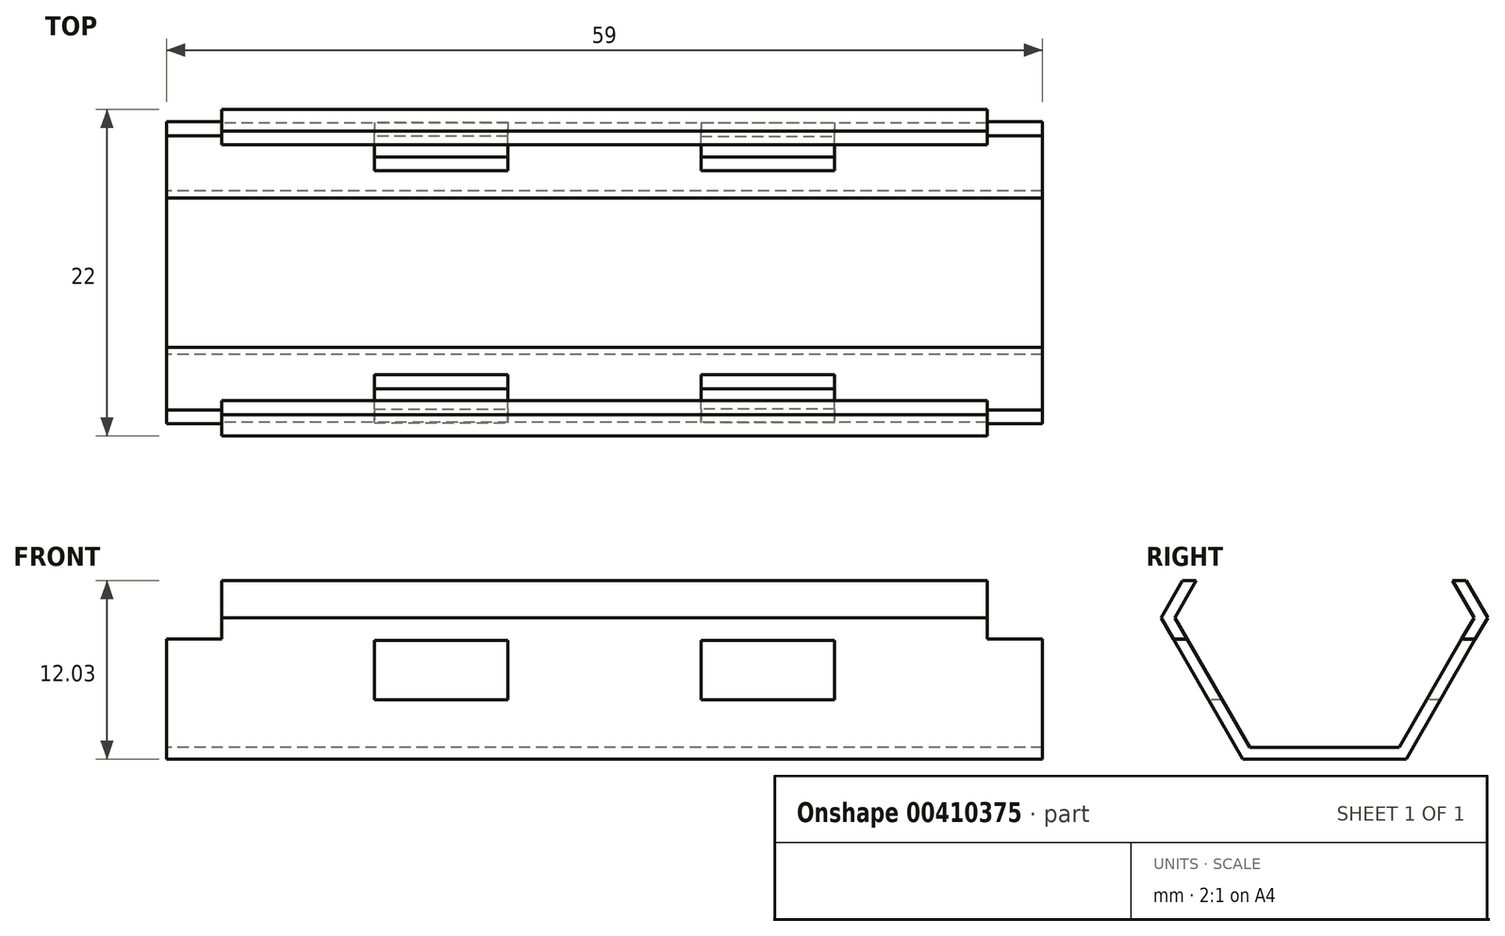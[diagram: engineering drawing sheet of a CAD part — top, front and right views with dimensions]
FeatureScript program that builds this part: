
annotation { "Feature Type Name" : "Feature", "Feature Type Description" : "" }
export const myFeature = defineFeature(function(context is Context, id is Id, definition is map)
    precondition{}
    {
        {
            var Q0;
            Q0=qCreatedBy(makeId("Right.planeOp"),FACE);
            var sketch = newSketch(context, id + "F0", { "sketchPlane" : qUnion([Q0])});
            skCircle(sketch, "E0.cCircle", {"center": v(0, 0) * mm, "radius": 9.53 * mm, "construction": true});
            skLineSegment(sketch, "E0.0", {"start": v(5.5, 9.53) * mm, "end": v(11, 0) * mm});
            skLineSegment(sketch, "E0.1", {"start": v(11, 0) * mm, "end": v(5.5, -9.53) * mm});
            skLineSegment(sketch, "E0.2", {"start": v(5.5, -9.53) * mm, "end": v(-5.5, -9.53) * mm});
            skLineSegment(sketch, "E0.3", {"start": v(-5.5, -9.53) * mm, "end": v(-11, 0) * mm});
            skLineSegment(sketch, "E0.4", {"start": v(-11, 0) * mm, "end": v(-5.5, 9.53) * mm});
            skLineSegment(sketch, "E0.5", {"start": v(-5.5, 9.53) * mm, "end": v(5.5, 9.53) * mm});
            skPoint(sketch, "E0.0.midPoint", {"position": v(8.25, 4.76) * mm});
            skSolve(sketch);
        }
        {
            var Q0;
            Q0=qCreatedBy(makeId("Right.planeOp"),FACE);
            var sketch = newSketch(context, id + "F1", { "sketchPlane" : qUnion([Q0])});
            skLineSegment(sketch, "E1.0", {"start": v(-10.08, 0) * mm, "end": v(-5.04, 8.73) * mm});
            skLineSegment(sketch, "E1.1", {"start": v(5.04, 8.73) * mm, "end": v(10.08, 0) * mm});
            skLineSegment(sketch, "E1.2", {"start": v(10.08, 0) * mm, "end": v(5.04, -8.73) * mm});
            skLineSegment(sketch, "E1.3", {"start": v(-5.04, 8.73) * mm, "end": v(5.04, 8.73) * mm});
            skLineSegment(sketch, "E1.4", {"start": v(5.04, -8.73) * mm, "end": v(-5.04, -8.73) * mm});
            skLineSegment(sketch, "E1.5", {"start": v(-5.04, -8.73) * mm, "end": v(-10.08, 0) * mm});
            skSolve(sketch);
        }
        {
            var Q0;
            Q0=makeQuery(id+"F0.imprint","IMPRINT",FACE,{"disambiguationData":[TD([[makeQuery(id+"F0.imprint","IMPRINT",EDGE,{"derivedFrom":sQuery(id+"F0.wireOp",EDGE,"E0.0")}),-1.0]])]});
            extrude(context, id + "F2", {"entities" : qUnion([Q0]), "endBound" : BoundingType.SYMMETRIC, "depth" : 59 * mm});
        }
        {
            var Q0;
            Q0 = qSketchRegion(id + "F1", true);
            extrude(context, id + "F3", {"entities" : qUnion([Q0]), "operationType" : NewBodyOperationType.REMOVE, "endBound" : BoundingType.SYMMETRIC, "depth" : 60 * mm});
        }
        {
            var Q0;
            Q0=makeQuery(id+"F0.imprint","IMPRINT",FACE,{"disambiguationData":[TD([[makeQuery(id+"F0.imprint","IMPRINT",EDGE,{"derivedFrom":sQuery(id+"F0.wireOp",EDGE,"E0.0")}),-1.0]])]});
            var sketch = newSketch(context, id + "F4", { "sketchPlane" : qUnion([Q0])});
            skLineSegment(sketch, "E2.bottom", {"start": v(-12.38, -9.5) * mm, "end": v(12.27, -9.5) * mm});
            skLineSegment(sketch, "E2.top", {"start": v(-12.38, 2.5) * mm, "end": v(12.27, 2.5) * mm});
            skLineSegment(sketch, "E2.left", {"start": v(-12.38, -9.5) * mm, "end": v(-12.38, 2.5) * mm});
            skLineSegment(sketch, "E2.right", {"start": v(12.27, -9.5) * mm, "end": v(12.27, 2.5) * mm});
            skPoint(sketch, "E3.MirrorCS.end.orphan", {"position": v(12.27, 2.5) * mm});
            skPoint(sketch, "E3.MirrorCS.start.orphan", {"position": v(36.91, 2.5) * mm});
            skLineSegment(sketch, "E4.MirrorCS", {"start": v(12.27, 14.5) * mm, "end": v(12.27, 2.5) * mm});
            skLineSegment(sketch, "E5.MirrorCS", {"start": v(-12.38, 14.5) * mm, "end": v(12.27, 14.5) * mm});
            skLineSegment(sketch, "E6.MirrorCS", {"start": v(-12.38, 14.5) * mm, "end": v(-12.38, 2.5) * mm});
            skSolve(sketch);
        }
        {
            var Q0;
            {var subQ4=sQuery(id+"F4.wireOp",EDGE,"E4.MirrorCS");Q0=makeQuery(id+"F4.imprint","IMPRINT",FACE,{"disambiguationData":[TD([[makeQuery(id+"F4.imprint","IMPRINT",EDGE,{"derivedFrom":subQ4}),-1.0]])]});}
            var Q1;
            {var subQ5=makeQuery(id+"F0.imprint","IMPRINT",EDGE,{"derivedFrom":sQuery(id+"F0.wireOp",EDGE,"E0.5")});Q1=makeQuery(id+"F4.imprint","IMPRINT",FACE,{"disambiguationData":[TD([[makeQuery(id+"F4.imprint","IMPRINT",EDGE,{"derivedFrom":subQ5}),-1.0]])]});}
            extrude(context, id + "F5", {"entities" : qUnion([Q0, Q1]), "operationType" : NewBodyOperationType.REMOVE, "endBound" : BoundingType.SYMMETRIC, "depth" : 91.7 * mm});
        }
        {
            var Q0;
            Q0=qCreatedBy(makeId("Front.planeOp"),FACE);
            var sketch = newSketch(context, id + "F6", { "sketchPlane" : qUnion([Q0])});
            skLineSegment(sketch, "E7.bottom", {"start": v(15.5, -1.53) * mm, "end": v(6.5, -1.53) * mm});
            skLineSegment(sketch, "E7.top", {"start": v(15.5, -5.53) * mm, "end": v(6.5, -5.53) * mm});
            skLineSegment(sketch, "E7.left", {"start": v(15.5, -1.53) * mm, "end": v(15.5, -5.53) * mm});
            skLineSegment(sketch, "E7.right", {"start": v(6.5, -1.53) * mm, "end": v(6.5, -5.53) * mm});
            skLineSegment(sketch, "E8.MirrorCS", {"start": v(-15.5, -5.53) * mm, "end": v(-6.5, -5.53) * mm});
            skLineSegment(sketch, "E9.MirrorCS", {"start": v(-15.5, -1.53) * mm, "end": v(-6.5, -1.53) * mm});
            skLineSegment(sketch, "E10.MirrorCS", {"start": v(-15.5, -1.53) * mm, "end": v(-15.5, -5.53) * mm});
            skLineSegment(sketch, "E11.MirrorCS", {"start": v(-6.5, -1.53) * mm, "end": v(-6.5, -5.53) * mm});
            skSolve(sketch);
        }
        {
            var Q0;
            Q0 = qSketchRegion(id + "F6", true);
            extrude(context, id + "F7", {"entities" : qUnion([Q0]), "operationType" : NewBodyOperationType.REMOVE, "endBound" : BoundingType.SYMMETRIC, "oppositeDirection" : true, "depth" : 25 * mm});
        }
        {
            var Q0;
            Q0=qCreatedBy(makeId("Front.planeOp"),FACE);
            var sketch = newSketch(context, id + "F8", { "sketchPlane" : qUnion([Q0])});
            skLineSegment(sketch, "E12.bottom", {"start": v(-29.77, 2.55) * mm, "end": v(-25.77, 2.55) * mm});
            skLineSegment(sketch, "E12.top", {"start": v(-29.77, -1.45) * mm, "end": v(-25.77, -1.45) * mm});
            skLineSegment(sketch, "E12.left", {"start": v(-29.77, 2.55) * mm, "end": v(-29.77, -1.45) * mm});
            skLineSegment(sketch, "E12.right", {"start": v(-25.77, 2.55) * mm, "end": v(-25.77, -1.45) * mm});
            skLineSegment(sketch, "E13.MirrorCS", {"start": v(25.77, 2.55) * mm, "end": v(25.77, -1.45) * mm});
            skLineSegment(sketch, "E14.MirrorCS", {"start": v(29.77, 2.55) * mm, "end": v(29.77, -1.45) * mm});
            skLineSegment(sketch, "E15.MirrorCS", {"start": v(29.77, -1.45) * mm, "end": v(25.77, -1.45) * mm});
            skLineSegment(sketch, "E16.MirrorCS", {"start": v(29.77, 2.55) * mm, "end": v(25.77, 2.55) * mm});
            skSolve(sketch);
        }
        {
            var Q0;
            Q0 = qSketchRegion(id + "F8", true);
            extrude(context, id + "F9", {"entities" : qUnion([Q0]), "operationType" : NewBodyOperationType.REMOVE, "endBound" : BoundingType.SYMMETRIC, "oppositeDirection" : true, "depth" : 25 * mm});
        }
    });
